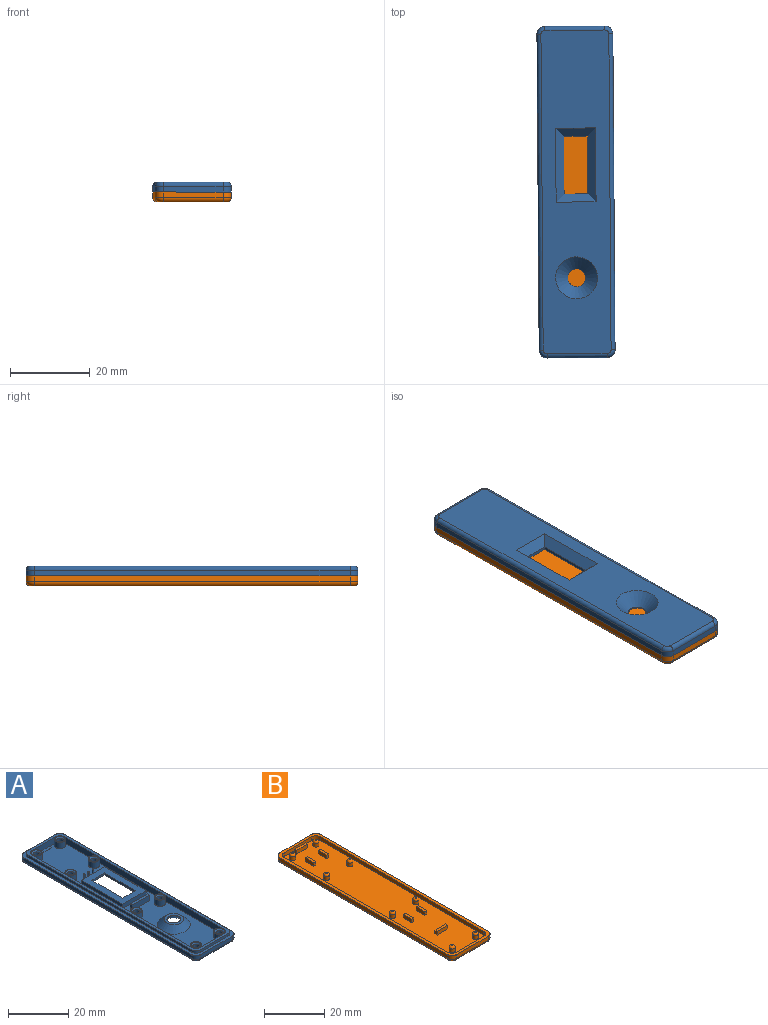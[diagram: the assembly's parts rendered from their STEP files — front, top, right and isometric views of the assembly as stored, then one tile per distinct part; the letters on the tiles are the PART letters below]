
ASSEMBLY  parts=2 mates=1
PART A: 108 faces, bbox 19.3x83.3x3.5 mm
  f0: plane 79x15mm, normal (0,0,1), area 772.4mm2, adj f2,f13,f14,f15,f16,f17,f21,f25
  f1: plane 81x17mm, normal (0,0,-1), area 1104.6mm2, adj f86,f87,f88,f89,f90,f92,f93,f94
  f2: plane 11x2.5mm, normal (0,-1,0), area 27mm2, adj f0,f12,f17,f18,f52,f79,f81
  f3: plane 83x19mm, normal (0,0,1), area 200mm2, adj f4,f5,f6,f7,f8,f9,f10,f11
  f4: plane 15x1.5mm, normal (0,-1,0), area 22.5mm2, adj f3,f82,f85,f95
  f5: plane 79x1.5mm, normal (1,0,0), area 118.5mm2, adj f3,f82,f83,f99
  f6: plane 15x1.5mm, normal (0,1,0), area 22.5mm2, adj f3,f83,f84,f96
  f7: plane 79x1.5mm, normal (-1,0,0), area 118.5mm2, adj f3,f84,f85,f92
  f8: plane 13x1mm, normal (0,-1,0), area 13mm2, adj f3,f12,f74,f77
  f9: plane 77x1mm, normal (1,0,0), area 77mm2, adj f3,f12,f74,f75
  f10: plane 13x1mm, normal (0,1,0), area 13mm2, adj f3,f12,f75,f76
  f11: plane 77x1mm, normal (-1,0,0), area 77mm2, adj f3,f12,f76,f77
  f12: plane 81x17mm, normal (0,0,1), area 192mm2, adj f2,f8,f9,f10,f11,f13,f14,f15
  f13: plane 75x2.5mm, normal (1,0,0), area 187.5mm2, adj f0,f12,f80,f81
  f14: plane 11x2.5mm, normal (0,1,0), area 27.5mm2, adj f0,f12,f78,f80
  f15: plane 75x2.5mm, normal (-1,0,0), area 187.5mm2, adj f0,f12,f78,f79
  f16: plane 5x0.1mm, normal (0,-1,0), area 0.5mm2, adj f0,f17,f18,f52
  f17: plane 1x0.1mm, normal (-1,0,0), area 0.1mm2, adj f0,f2,f16,f18
  f18: plane 5x1mm, normal (0,0,1), area 5mm2, adj f2,f16,f17,f52
  f19: plane 3.7x3.7mm, normal (0,0,1), area 2.2mm2, adj f21,f104
  f20: cylinder r=1.15mm len=2.3mm, axis (0,0,-1), area 14.5mm2, adj f22,f104
  f21: cylinder r=1.85mm len=3.7mm, axis (0,0,-1), area 29.1mm2, adj f0,f19
  f22: plane 2.3x2.3mm, normal (0,0,1), area 4.2mm2, adj f20
  f23: plane 3.7x3.7mm, normal (0,0,1), area 2.2mm2, adj f25,f107
  f24: cylinder r=1.15mm len=2.3mm, axis (0,0,-1), area 14.5mm2, adj f26,f107
  f25: cylinder r=1.85mm len=3.7mm, axis (0,0,-1), area 29.1mm2, adj f0,f23
  f26: plane 2.3x2.3mm, normal (0,0,1), area 4.2mm2, adj f24
  f27: plane 3.7x3.7mm, normal (0,0,1), area 2.2mm2, adj f29,f106
  f28: cylinder r=1.15mm len=2.3mm, axis (0,0,-1), area 14.5mm2, adj f30,f106
  f29: cylinder r=1.85mm len=3.7mm, axis (0,0,-1), area 29.1mm2, adj f0,f27
  f30: plane 2.3x2.3mm, normal (0,0,1), area 4.2mm2, adj f28
  f31: plane 3.7x3.7mm, normal (0,0,1), area 2.2mm2, adj f33,f105
  f32: cylinder r=1.15mm len=2.3mm, axis (0,0,-1), area 14.5mm2, adj f34,f105
  f33: cylinder r=1.85mm len=3.7mm, axis (0,0,-1), area 29.1mm2, adj f0,f31
  f34: plane 2.3x2.3mm, normal (0,0,1), area 4.2mm2, adj f32
  f35: plane 6x0.8mm, normal (0,1,0), area 4.8mm2, adj f37,f38,f69,f89
  f36: plane 6x0.8mm, normal (0,-1,0), area 4.8mm2, adj f37,f38,f69,f86
  f37: plane 14.5x0.8mm, normal (1,0,0), area 11.6mm2, adj f35,f36,f38,f87
  f38: plane 19.5x11mm, normal (0,0,1), area 127.5mm2, adj f35,f36,f37,f39,f40,f41,f69,f70
  f39: plane 11x1.8mm, normal (0,1,0), area 19.8mm2, adj f0,f38,f40,f70
  f40: plane 19.5x1.8mm, normal (-1,0,0), area 35.1mm2, adj f0,f38,f39,f41
  f41: plane 11x1.8mm, normal (0,-1,0), area 19.8mm2, adj f0,f38,f40,f70
  f42: cylinder r=2.25mm len=4.5mm, axis (0,0,1), area 3.5mm2, adj f43,f90
  f43: plane 6.5x6.5mm, normal (0,0,1), area 17.3mm2, adj f42,f91
  f44: plane 0.5x0.5mm, normal (0,0,1), area 0.2mm2, adj f45
  f45: cylinder r=0.25mm len=1.5mm, axis (0,0,-1), area 2.4mm2, adj f0,f44
  f46: plane 0.5x0.5mm, normal (0,0,1), area 0.2mm2, adj f47
  f47: cylinder r=0.25mm len=1.5mm, axis (0,0,-1), area 2.4mm2, adj f0,f46
  f48: plane 8x1mm, normal (0,0,1), area 8mm2, adj f49,f50,f51,f73
  f49: plane 8x2.25mm, normal (0,1,0), area 18mm2, adj f0,f48,f50,f73
  f50: plane 2.25x1mm, normal (-1,0,0), area 2.2mm2, adj f0,f48,f49,f51
  f51: plane 8x2.25mm, normal (0,-1,0), area 18mm2, adj f0,f48,f50,f73
  f52: plane 1x0.1mm, normal (1,0,0), area 0.1mm2, adj f0,f2,f16,f18
  f53: plane 3.7x3.7mm, normal (0,0,1), area 2.2mm2, adj f54,f100
  f54: cylinder r=1.85mm len=3.7mm, axis (0,0,-1), area 29.1mm2, adj f0,f53
  f55: cylinder r=1.15mm len=2.3mm, axis (0,0,-1), area 14.5mm2, adj f56,f100
  f56: plane 2.3x2.3mm, normal (0,0,1), area 4.2mm2, adj f55
  f57: plane 3.7x3.7mm, normal (0,0,1), area 2.2mm2, adj f58,f103
  f58: cylinder r=1.85mm len=3.7mm, axis (0,0,-1), area 29.1mm2, adj f0,f57
  f59: cylinder r=1.15mm len=2.3mm, axis (0,0,-1), area 14.5mm2, adj f60,f103
  f60: plane 2.3x2.3mm, normal (0,0,1), area 4.2mm2, adj f59
  f61: plane 3.7x3.7mm, normal (0,0,1), area 2.2mm2, adj f62,f102
  f62: cylinder r=1.85mm len=3.7mm, axis (0,0,-1), area 29.1mm2, adj f0,f61
  f63: cylinder r=1.15mm len=2.3mm, axis (0,0,-1), area 14.5mm2, adj f64,f102
  f64: plane 2.3x2.3mm, normal (0,0,1), area 4.2mm2, adj f63
  f65: plane 3.7x3.7mm, normal (0,0,1), area 2.2mm2, adj f66,f101
  f66: cylinder r=1.85mm len=3.7mm, axis (0,0,-1), area 29.1mm2, adj f0,f65
  f67: cylinder r=1.15mm len=2.3mm, axis (0,0,-1), area 14.5mm2, adj f68,f101
  f68: plane 2.3x2.3mm, normal (0,0,1), area 4.2mm2, adj f67
  f69: plane 14.5x0.8mm, normal (-1,0,0), area 11.6mm2, adj f35,f36,f38,f88
  f70: plane 19.5x1.8mm, normal (1,0,0), area 35.1mm2, adj f0,f38,f39,f41
  f71: plane 0.5x0.5mm, normal (0,0,1), area 0.2mm2, adj f72
  f72: cylinder r=0.25mm len=1.5mm, axis (0,0,-1), area 2.4mm2, adj f0,f71
  f73: plane 2.25x1mm, normal (1,0,0), area 2.2mm2, adj f0,f48,f49,f51
  f74: cylinder r=2mm len=2mm, axis (0,0,1), area 3.1mm2, adj f3,f8,f9,f12
  f75: cylinder r=2mm len=2mm, axis (0,0,-1), area 3.1mm2, adj f3,f9,f10,f12
  f76: cylinder r=2mm len=2mm, axis (0,0,1), area 3.1mm2, adj f3,f10,f11,f12
  f77: cylinder r=2mm len=2mm, axis (0,0,-1), area 3.1mm2, adj f3,f8,f11,f12
  f78: cylinder r=2mm len=2.5mm, axis (0,0,1), area 7.9mm2, adj f0,f12,f14,f15
  f79: cylinder r=2mm len=2.5mm, axis (0,0,-1), area 7.9mm2, adj f0,f2,f12,f15
  f80: cylinder r=2mm len=2.5mm, axis (0,0,-1), area 7.9mm2, adj f0,f12,f13,f14
  f81: cylinder r=2mm len=2.5mm, axis (0,0,1), area 7.9mm2, adj f0,f2,f12,f13
  f82: cylinder r=2mm len=2mm, axis (0,0,1), area 4.7mm2, adj f3,f4,f5,f97
  f83: cylinder r=2mm len=2mm, axis (0,0,-1), area 4.7mm2, adj f3,f5,f6,f98
  f84: cylinder r=2mm len=2mm, axis (0,0,1), area 4.7mm2, adj f3,f6,f7,f94
  f85: cylinder r=2mm len=2mm, axis (0,0,-1), area 4.7mm2, adj f3,f4,f7,f93
  f86: plane 10x2mm, normal (0,-0.71,-0.71), area 22.6mm2, adj f1,f36,f87,f88
  f87: plane 18.5x2mm, normal (0.71,0,-0.71), area 46.7mm2, adj f1,f37,f86,f89
  f88: plane 18.5x2mm, normal (-0.71,0,-0.71), area 46.7mm2, adj f1,f69,f86,f89
  f89: plane 10x2mm, normal (0,0.71,-0.71), area 22.6mm2, adj f1,f35,f87,f88
  f90: cone r=2.25mm half-angle=45deg, axis (0,0,-1), area 100mm2, adj f1,f42
  f91: cone r=3.25mm half-angle=45deg, axis (0,0,-1), area 87.5mm2, adj f0,f43
  f92: cylinder r=1mm len=79mm, axis (0,-1,0), area 124.1mm2, adj f1,f7,f93,f94
  f93: torus R=1mm, axis (0,0,1), area 4mm2, adj f1,f85,f92,f95
  f94: torus R=1mm, axis (0,0,1), area 4mm2, adj f1,f84,f92,f96
  f95: cylinder r=1mm len=15mm, axis (1,0,0), area 23.6mm2, adj f1,f4,f93,f97
  f96: cylinder r=1mm len=15mm, axis (-1,0,0), area 23.6mm2, adj f1,f6,f94,f98
  f97: torus R=1mm, axis (0,0,1), area 4mm2, adj f1,f82,f95,f99
  f98: torus R=1mm, axis (0,0,1), area 4mm2, adj f1,f83,f96,f99
  f99: cylinder r=1mm len=79mm, axis (0,1,0), area 124.1mm2, adj f1,f5,f97,f98
  f100: torus R=1.65mm, axis (0,0,1), area 6.6mm2, adj f53,f55
  f101: torus R=1.65mm, axis (0,0,1), area 6.6mm2, adj f65,f67
  f102: torus R=1.65mm, axis (0,0,1), area 6.6mm2, adj f61,f63
  f103: torus R=1.65mm, axis (0,0,1), area 6.6mm2, adj f57,f59
  f104: torus R=1.65mm, axis (0,0,1), area 6.6mm2, adj f19,f20
  f105: torus R=1.65mm, axis (0,0,1), area 6.6mm2, adj f31,f32
  f106: torus R=1.65mm, axis (0,0,1), area 6.6mm2, adj f27,f28
  f107: torus R=1.65mm, axis (0,0,1), area 6.6mm2, adj f23,f24
PART B: 81 faces, bbox 19.3x83.3x3.3 mm
  f0: plane 81x17mm, normal (0,0,1), area 1322.2mm2, adj f7,f8,f9,f10,f12,f13,f14,f16
  f1: plane 15x1.5mm, normal (0,-1,0), area 22.5mm2, adj f5,f41,f44,f76
  f2: plane 79x1.5mm, normal (1,0,0), area 118.5mm2, adj f5,f41,f42,f73
  f3: plane 15x1.5mm, normal (0,1,0), area 22.5mm2, adj f5,f42,f43,f77
  f4: plane 79x1.5mm, normal (-1,0,0), area 118.5mm2, adj f5,f43,f44,f80
  f5: plane 83x19mm, normal (0,0,1), area 200mm2, adj f1,f2,f3,f4,f7,f8,f9,f10
  f6: plane 81x17mm, normal (0,0,-1), area 1376.1mm2, adj f73,f74,f75,f76,f77,f78,f79,f80
  f7: plane 77x1.5mm, normal (-1,0,0), area 115.5mm2, adj f0,f5,f37,f38
  f8: plane 13x1.5mm, normal (0,1,0), area 19.5mm2, adj f0,f5,f37,f39
  f9: plane 13x1.5mm, normal (0,-1,0), area 19.5mm2, adj f0,f5,f38,f40
  f10: plane 77x1.5mm, normal (1,0,0), area 115.5mm2, adj f0,f5,f39,f40
  f11: plane 5.1x1mm, normal (0,0,1), area 5.1mm2, adj f12,f13,f14,f72
  f12: plane 5.1x1.5mm, normal (0,1,0), area 7.7mm2, adj f0,f11,f14,f72
  f13: plane 5.1x1.5mm, normal (0,-1,0), area 7.7mm2, adj f0,f11,f14,f72
  f14: plane 1.5x1mm, normal (-1,0,0), area 1.5mm2, adj f0,f11,f12,f13
  f15: plane 5.1x1mm, normal (0,0,1), area 5.1mm2, adj f16,f17,f18,f71
  f16: plane 5.1x1.5mm, normal (0,1,0), area 7.7mm2, adj f0,f15,f18,f71
  f17: plane 5.1x1.5mm, normal (0,-1,0), area 7.7mm2, adj f0,f15,f18,f71
  f18: plane 1.5x1mm, normal (-1,0,0), area 1.5mm2, adj f0,f15,f16,f17
  f19: plane 4x1mm, normal (0,0,1), area 4mm2, adj f20,f21,f22,f23
  f20: plane 4x1.5mm, normal (-1,0,0), area 6mm2, adj f0,f19,f21,f22
  f21: plane 1.5x1mm, normal (0,-1,0), area 1.5mm2, adj f0,f19,f20,f23
  f22: plane 1.5x1mm, normal (0,1,0), area 1.5mm2, adj f0,f19,f20,f23
  f23: plane 4x1.5mm, normal (1,0,0), area 6mm2, adj f0,f19,f21,f22
  f24: plane 4x1mm, normal (0,0,1), area 4mm2, adj f25,f26,f27,f28
  f25: plane 4x1.5mm, normal (-1,0,0), area 6mm2, adj f0,f24,f26,f27
  f26: plane 1.5x1mm, normal (0,-1,0), area 1.5mm2, adj f0,f24,f25,f28
  f27: plane 1.5x1mm, normal (0,1,0), area 1.5mm2, adj f0,f24,f25,f28
  f28: plane 4x1.5mm, normal (1,0,0), area 6mm2, adj f0,f24,f26,f27
  f29: cylinder r=1mm len=2mm, axis (0,0,-1), area 9.4mm2, adj f0,f45
  f30: plane 0.5x0.5mm, normal (0,0,1), area 0.2mm2, adj f45
  f31: cylinder r=1mm len=2mm, axis (0,0,-1), area 9.4mm2, adj f0,f48
  f32: plane 0.5x0.5mm, normal (0,0,1), area 0.2mm2, adj f48
  f33: cylinder r=1mm len=2mm, axis (0,0,-1), area 9.4mm2, adj f0,f47
  f34: plane 0.5x0.5mm, normal (0,0,1), area 0.2mm2, adj f47
  f35: cylinder r=1mm len=2mm, axis (0,0,-1), area 9.4mm2, adj f0,f46
  f36: plane 0.5x0.5mm, normal (0,0,1), area 0.2mm2, adj f46
  f37: cylinder r=2mm len=2mm, axis (0,0,1), area 4.7mm2, adj f0,f5,f7,f8
  f38: cylinder r=2mm len=2mm, axis (0,0,-1), area 4.7mm2, adj f0,f5,f7,f9
  f39: cylinder r=2mm len=2mm, axis (0,0,-1), area 4.7mm2, adj f0,f5,f8,f10
  f40: cylinder r=2mm len=2mm, axis (0,0,1), area 4.7mm2, adj f0,f5,f9,f10
  f41: cylinder r=2mm len=2mm, axis (0,0,1), area 4.7mm2, adj f1,f2,f5,f74
  f42: cylinder r=2mm len=2mm, axis (0,0,-1), area 4.7mm2, adj f2,f3,f5,f75
  f43: cylinder r=2mm len=2mm, axis (0,0,1), area 4.7mm2, adj f3,f4,f5,f79
  f44: cylinder r=2mm len=2mm, axis (0,0,-1), area 4.7mm2, adj f1,f4,f5,f78
  f45: torus R=0.25mm, axis (0,0,1), area 5.4mm2, adj f29,f30
  f46: torus R=0.25mm, axis (0,0,1), area 5.4mm2, adj f35,f36
  f47: torus R=0.25mm, axis (0,0,1), area 5.4mm2, adj f33,f34
  f48: torus R=0.25mm, axis (0,0,1), area 5.4mm2, adj f31,f32
  f49: plane 0.5x0.5mm, normal (0,0,1), area 0.2mm2, adj f50
  f50: torus R=0.25mm, axis (0,0,1), area 5.4mm2, adj f49,f51
  f51: cylinder r=1mm len=2mm, axis (0,0,-1), area 9.4mm2, adj f0,f50
  f52: plane 0.5x0.5mm, normal (0,0,1), area 0.2mm2, adj f53
  f53: torus R=0.25mm, axis (0,0,1), area 5.4mm2, adj f52,f54
  f54: cylinder r=1mm len=2mm, axis (0,0,-1), area 9.4mm2, adj f0,f53
  f55: plane 0.5x0.5mm, normal (0,0,1), area 0.2mm2, adj f56
  f56: torus R=0.25mm, axis (0,0,1), area 5.4mm2, adj f55,f57
  f57: cylinder r=1mm len=2mm, axis (0,0,-1), area 9.4mm2, adj f0,f56
  f58: plane 0.5x0.5mm, normal (0,0,1), area 0.2mm2, adj f59
  f59: torus R=0.25mm, axis (0,0,1), area 5.4mm2, adj f58,f60
  f60: cylinder r=1mm len=2mm, axis (0,0,-1), area 9.4mm2, adj f0,f59
  f61: plane 4x1mm, normal (0,0,1), area 4mm2, adj f62,f63,f64,f65
  f62: plane 4x1.5mm, normal (-1,0,0), area 6mm2, adj f0,f61,f63,f64
  f63: plane 1.5x1mm, normal (0,1,0), area 1.5mm2, adj f0,f61,f62,f65
  f64: plane 1.5x1mm, normal (0,-1,0), area 1.5mm2, adj f0,f61,f62,f65
  f65: plane 4x1.5mm, normal (1,0,0), area 6mm2, adj f0,f61,f63,f64
  f66: plane 4x1mm, normal (0,0,1), area 4mm2, adj f67,f68,f69,f70
  f67: plane 4x1.5mm, normal (-1,0,0), area 6mm2, adj f0,f66,f68,f69
  f68: plane 1.5x1mm, normal (0,1,0), area 1.5mm2, adj f0,f66,f67,f70
  f69: plane 1.5x1mm, normal (0,-1,0), area 1.5mm2, adj f0,f66,f67,f70
  f70: plane 4x1.5mm, normal (1,0,0), area 6mm2, adj f0,f66,f68,f69
  f71: plane 1.5x1mm, normal (1,0,0), area 1.5mm2, adj f0,f15,f16,f17
  f72: plane 1.5x1mm, normal (1,0,0), area 1.5mm2, adj f0,f11,f12,f13
  f73: cylinder r=1mm len=79mm, axis (0,1,0), area 124.1mm2, adj f2,f6,f74,f75
  f74: torus R=1mm, axis (0,0,1), area 4mm2, adj f6,f41,f73,f76
  f75: torus R=1mm, axis (0,0,1), area 4mm2, adj f6,f42,f73,f77
  f76: cylinder r=1mm len=15mm, axis (1,0,0), area 23.6mm2, adj f1,f6,f74,f78
  f77: cylinder r=1mm len=15mm, axis (-1,0,0), area 23.6mm2, adj f3,f6,f75,f79
  f78: torus R=1mm, axis (0,0,1), area 4mm2, adj f6,f44,f76,f80
  f79: torus R=1mm, axis (0,0,1), area 4mm2, adj f6,f43,f77,f80
  f80: cylinder r=1mm len=79mm, axis (0,-1,0), area 124.1mm2, adj f4,f6,f78,f79
PLACE A rot(axis=(0,-1,0),180deg) t=(-1.33,4.08,-8.98)mm
PLACE B rot(axis=(0,0,1),0.4deg) t=(-1.33,4.08,-13.98)mm
MATE fastened A.f3 <-> B.f5  axis (0,0,-1) through (8.45,-35.36,-11.48)mm
